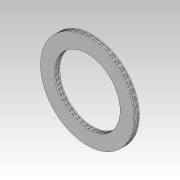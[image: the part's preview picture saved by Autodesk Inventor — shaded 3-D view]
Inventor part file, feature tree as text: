
AUTODESK INVENTOR PART (.ipt)
format: ipt  version: 2020 (Build 240168000, 168)  size: 527,872 bytes
history: native  units: mm
features: sketch x3, revolve x2, extrude x1, pattern_circular x1
ambient origin geometry x8: Origin, YZ Plane, XZ Plane, XY Plane, X Axis, Y Axis, Z Axis, Center Point
bodies: Solid1 (feature_tree)
feature tree (7):
  extrude  "Extrusion1"  Depth=60.0mm
  revolve  "Revolution1"  [1 undecoded]
  pattern_circular  "Circular Pattern1"  Count=50 Angle=360.0deg
  revolve  "Revolution2"  [1 undecoded]
  sketch  "Sketch1"  dims[d0=60.0mm d1=85.0mm]
  sketch  "Sketch2"  dims[d2=1.0mm d3=0.0mm d4=1.5mm]
  sketch  "Sketch3"  dims[d5=90.0deg d6=500.0mm d7=360.0deg d9=1.0mm d10=1.0mm d11=90.0deg]
note: 2 required parameter values undecoded (feature->parameter linkage not recoverable at this tier; creation-order binding heuristic only, values carry confidence <= 0.55)
